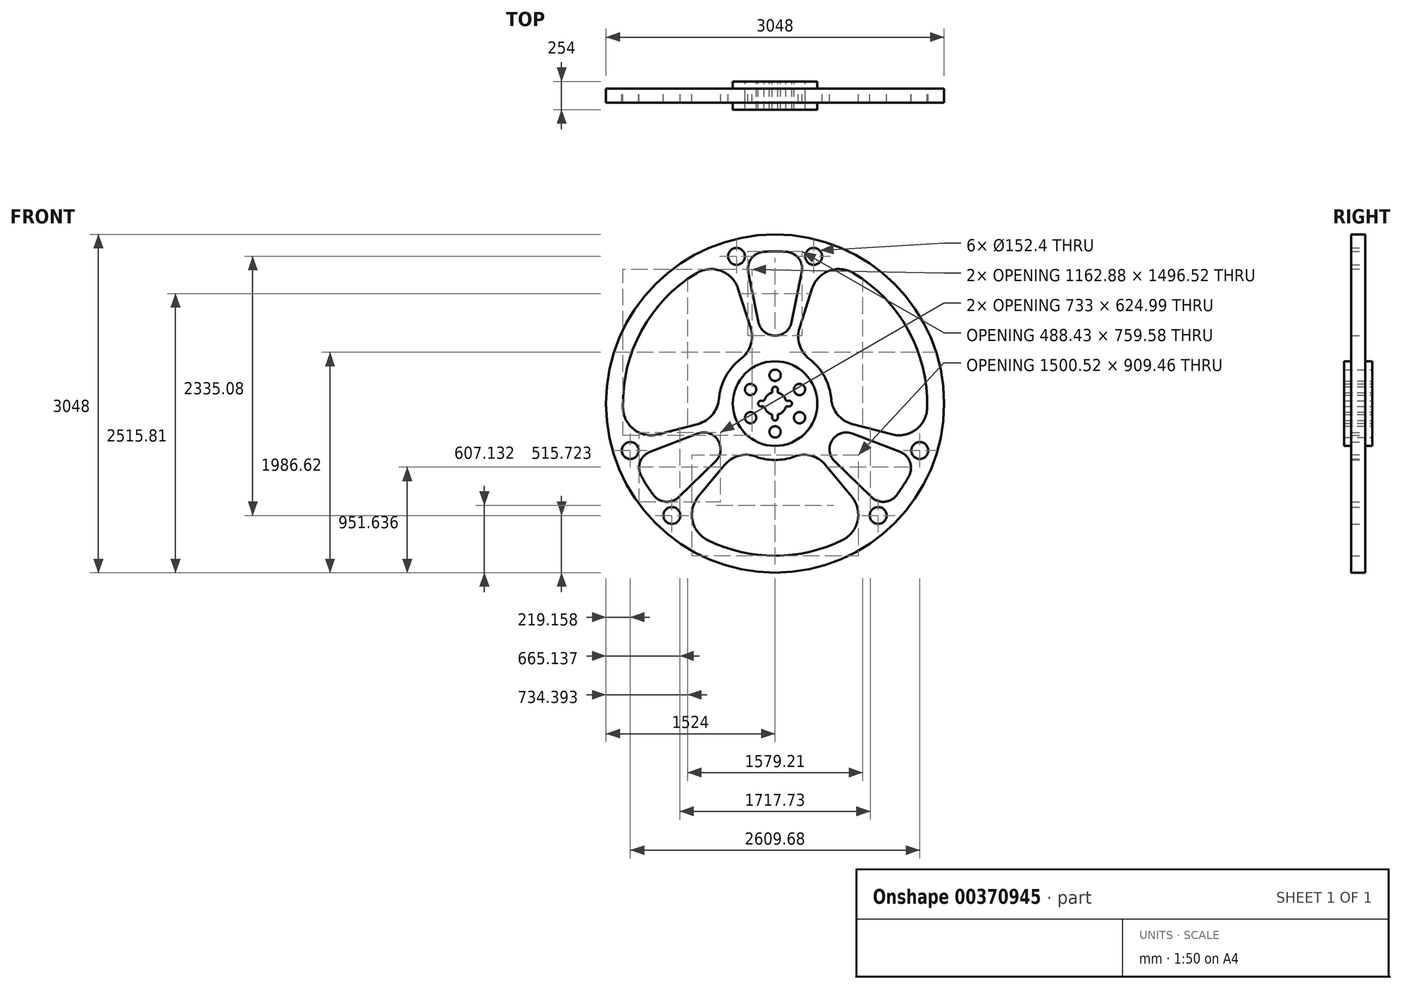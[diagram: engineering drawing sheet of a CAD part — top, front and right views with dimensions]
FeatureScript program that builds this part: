
annotation { "Feature Type Name" : "Feature", "Feature Type Description" : "" }
export const myFeature = defineFeature(function(context is Context, id is Id, definition is map)
    precondition{}
    {
        {
            var Q0;
            Q0=qCreatedBy(makeId("Front.planeOp"),FACE);
            var sketch = newSketch(context, id + "F0", { "sketchPlane" : qUnion([Q0])});
            skCircle(sketch, "E0", {"center": v(0, 0) * mm, "radius": 1524 * mm});
            skArc(sketch, "E1", {"start": v(-1207.5, -650.55) * mm, "mid": v(-1155.08, -739.64) * mm, "end": v(-1096.1, -824.54) * mm});
            skArc(sketch, "E2", {"start": v(-173.99, -477.28) * mm, "mid": v(0, -508) * mm, "end": v(173.99, -477.28) * mm});
            skCircle(sketch, "E3", {"center": v(-347.67, 1326.8) * mm, "radius": 76.2 * mm});
            skCircle(sketch, "E4", {"center": v(347.67, 1326.8) * mm, "radius": 76.2 * mm});
            skCircle(sketch, "E5", {"center": v(929.87, -1008.28) * mm, "radius": 76.2 * mm});
            skCircle(sketch, "E6", {"center": v(-929.87, -1008.28) * mm, "radius": 76.2 * mm});
            skCircle(sketch, "E7", {"center": v(-1304.84, -422.7) * mm, "radius": 76.2 * mm});
            skCircle(sketch, "E8", {"center": v(1304.84, -422.7) * mm, "radius": 76.2 * mm});
            skLineSegment(sketch, "E9", {"start": v(-420.82, 1305.45) * mm, "end": v(-419.52, 1301.42) * mm});
            skLineSegment(sketch, "E10", {"start": v(-273.45, 1344.06) * mm, "end": v(-272.6, 1339.92) * mm});
            skLineSegment(sketch, "E11", {"start": v(273.45, 1344.06) * mm, "end": v(272.6, 1339.92) * mm});
            skLineSegment(sketch, "E12", {"start": v(420.82, 1305.45) * mm, "end": v(419.52, 1301.42) * mm});
            skLineSegment(sketch, "E13", {"start": v(-1326.3, -349.58) * mm, "end": v(-1322.2, -348.5) * mm});
            skLineSegment(sketch, "E14", {"start": v(-1279.35, -494.5) * mm, "end": v(-1275.4, -492.98) * mm});
            skLineSegment(sketch, "E15", {"start": v(-984.43, -955.08) * mm, "end": v(-981.4, -952.13) * mm});
            skLineSegment(sketch, "E16", {"start": v(-872.44, -1058.36) * mm, "end": v(-869.75, -1055.1) * mm});
            skLineSegment(sketch, "E17", {"start": v(872.44, -1058.36) * mm, "end": v(869.75, -1055.1) * mm});
            skLineSegment(sketch, "E18", {"start": v(984.43, -955.08) * mm, "end": v(981.4, -952.13) * mm});
            skLineSegment(sketch, "E19", {"start": v(1279.35, -494.5) * mm, "end": v(1275.4, -492.98) * mm});
            skLineSegment(sketch, "E20", {"start": v(1326.3, -349.58) * mm, "end": v(1322.2, -348.5) * mm});
            skArc(sketch, "E21.trimOffspring", {"start": v(-609.08, -1228.95) * mm, "mid": v(0, -1371.6) * mm, "end": v(609.08, -1228.95) * mm});
            skArc(sketch, "E22.trimOffspring", {"start": v(1096.1, -824.54) * mm, "mid": v(1155.08, -739.64) * mm, "end": v(1207.5, -650.55) * mm});
            skArc(sketch, "E23.trimOffspring", {"start": v(1371.05, -39) * mm, "mid": v(1203.28, 658.33) * mm, "end": v(706.5, 1175.65) * mm});
            skArc(sketch, "E24.trimOffspring", {"start": v(103.3, 1367.7) * mm, "mid": v(0, 1371.6) * mm, "end": v(-103.3, 1367.7) * mm});
            skArc(sketch, "E25.trimOffspring", {"start": v(-706.5, 1175.65) * mm, "mid": v(-1203.28, 658.33) * mm, "end": v(-1371.05, -39) * mm});
            skArc(sketch, "E26.trimOffspring", {"start": v(-308.11, 403.9) * mm, "mid": v(-445.66, 243.83) * mm, "end": v(-506.29, 41.67) * mm});
            skArc(sketch, "E27.trimOffspring", {"start": v(506.29, 41.67) * mm, "mid": v(445.66, 243.83) * mm, "end": v(308.11, 403.9) * mm});
            skPoint(sketch, "E28.start.orphan", {"position": v(0, 1344.06) * mm});
            skArc(sketch, "E29", {"start": v(-103.3, 1367.7) * mm, "mid": v(-213.39, 1307.65) * mm, "end": v(-241.16, 1185.35) * mm});
            skArc(sketch, "E30", {"start": v(-333.92, 1035.86) * mm, "mid": v(-486.45, 1195.75) * mm, "end": v(-706.5, 1175.65) * mm});
            skArc(sketch, "E31", {"start": v(-1371.05, -39) * mm, "mid": v(-1269.3, -235.16) * mm, "end": v(-1052.41, -277.4) * mm});
            skArc(sketch, "E32", {"start": v(-1128.28, -436.12) * mm, "mid": v(-1216.3, -525.45) * mm, "end": v(-1207.5, -650.55) * mm});
            skArc(sketch, "E33", {"start": v(-1096.1, -824.54) * mm, "mid": v(-986.15, -884.86) * mm, "end": v(-868.19, -842.3) * mm});
            skArc(sketch, "E34", {"start": v(609.08, -1228.95) * mm, "mid": v(744.67, -1054.47) * mm, "end": v(692.28, -839.8) * mm});
            skArc(sketch, "E35", {"start": v(868.19, -842.3) * mm, "mid": v(986.15, -884.86) * mm, "end": v(1096.1, -824.54) * mm});
            skArc(sketch, "E36", {"start": v(1207.5, -650.55) * mm, "mid": v(1216.3, -525.45) * mm, "end": v(1128.28, -436.12) * mm});
            skArc(sketch, "E37", {"start": v(1052.41, -277.4) * mm, "mid": v(1269.3, -235.16) * mm, "end": v(1371.05, -39) * mm});
            skArc(sketch, "E38", {"start": v(706.5, 1175.65) * mm, "mid": v(486.45, 1195.75) * mm, "end": v(333.92, 1035.86) * mm});
            skArc(sketch, "E39", {"start": v(241.16, 1185.35) * mm, "mid": v(213.39, 1307.65) * mm, "end": v(103.3, 1367.7) * mm});
            skLineSegment(sketch, "E40.trimOffspring", {"start": v(-1052.41, -277.4) * mm, "end": v(-694.7, -183.1) * mm});
            skLineSegment(sketch, "E41.trimOffspring", {"start": v(-1128.28, -436.12) * mm, "end": v(-698.7, -270.07) * mm});
            skLineSegment(sketch, "E42.trimOffspring", {"start": v(-868.19, -842.3) * mm, "end": v(-537.63, -521.6) * mm});
            skLineSegment(sketch, "E43.trimOffspring", {"start": v(-692.28, -839.8) * mm, "end": v(-456.97, -554.35) * mm});
            skLineSegment(sketch, "E44.trimOffspring", {"start": v(692.28, -839.8) * mm, "end": v(456.97, -554.35) * mm});
            skLineSegment(sketch, "E45.trimOffspring", {"start": v(868.19, -842.3) * mm, "end": v(537.63, -521.6) * mm});
            skLineSegment(sketch, "E46.trimOffspring", {"start": v(1128.28, -436.12) * mm, "end": v(698.7, -270.07) * mm});
            skLineSegment(sketch, "E47.trimOffspring", {"start": v(1052.41, -277.4) * mm, "end": v(694.7, -183.1) * mm});
            skLineSegment(sketch, "E48.trimOffspring", {"start": v(333.92, 1035.86) * mm, "end": v(220.42, 683.77) * mm});
            skLineSegment(sketch, "E49.trimOffspring", {"start": v(241.16, 1185.35) * mm, "end": v(149.34, 734.03) * mm});
            skLineSegment(sketch, "E50.trimOffspring", {"start": v(-241.16, 1185.35) * mm, "end": v(-149.34, 734.03) * mm});
            skLineSegment(sketch, "E51.trimOffspring", {"start": v(-333.92, 1035.86) * mm, "end": v(-220.42, 683.77) * mm});
            skArc(sketch, "E52", {"start": v(-694.7, -183.1) * mm, "mid": v(-564.77, -100.66) * mm, "end": v(-506.29, 41.67) * mm});
            skArc(sketch, "E53", {"start": v(-308.11, 403.9) * mm, "mid": v(-219.79, 529.9) * mm, "end": v(-220.42, 683.77) * mm});
            skArc(sketch, "E54", {"start": v(220.42, 683.77) * mm, "mid": v(219.79, 529.9) * mm, "end": v(308.11, 403.9) * mm});
            skArc(sketch, "E55", {"start": v(506.29, 41.67) * mm, "mid": v(564.77, -100.66) * mm, "end": v(694.7, -183.1) * mm});
            skArc(sketch, "E56", {"start": v(456.97, -554.35) * mm, "mid": v(327.73, -470.84) * mm, "end": v(173.99, -477.28) * mm});
            skArc(sketch, "E57", {"start": v(-173.99, -477.28) * mm, "mid": v(-327.73, -470.84) * mm, "end": v(-456.97, -554.35) * mm});
            skArc(sketch, "E58", {"start": v(-537.63, -521.6) * mm, "mid": v(-515.4, -330.03) * mm, "end": v(-698.7, -270.07) * mm});
            skArc(sketch, "E59", {"start": v(-149.34, 734.03) * mm, "mid": v(0, 612.02) * mm, "end": v(149.34, 734.03) * mm});
            skArc(sketch, "E60.trimOffspring", {"start": v(-692.28, -839.8) * mm, "mid": v(-744.67, -1054.47) * mm, "end": v(-609.08, -1228.95) * mm});
            skCircle(sketch, "E61", {"center": v(0, 0) * mm, "radius": 381 * mm});
            skArc(sketch, "E62", {"start": v(698.7, -270.07) * mm, "mid": v(515.4, -330.03) * mm, "end": v(537.63, -521.6) * mm});
            skCircle(sketch, "E63", {"center": v(0, 254.8) * mm, "radius": 50.8 * mm});
            skCircle(sketch, "E64.1.0", {"center": v(-220.67, 127.4) * mm, "radius": 50.8 * mm});
            skCircle(sketch, "E64.2.0", {"center": v(-220.67, -127.4) * mm, "radius": 50.8 * mm});
            skCircle(sketch, "E64.3.0", {"center": v(0, -254.8) * mm, "radius": 50.8 * mm});
            skCircle(sketch, "E64.4.0", {"center": v(220.67, -127.4) * mm, "radius": 50.8 * mm});
            skCircle(sketch, "E64.5.0", {"center": v(220.67, 127.4) * mm, "radius": 50.8 * mm});
            skArc(sketch, "E65", {"start": v(-98.37, -25.4) * mm, "mid": v(-71.84, -71.84) * mm, "end": v(-25.4, -98.37) * mm});
            skArc(sketch, "E66", {"start": v(-127, 25.4) * mm, "mid": v(-152.4, 0) * mm, "end": v(-127, -25.4) * mm});
            skLineSegment(sketch, "E67", {"start": v(-127, 25.4) * mm, "end": v(-98.37, 25.4) * mm});
            skLineSegment(sketch, "E68", {"start": v(-127, -25.4) * mm, "end": v(-98.37, -25.4) * mm});
            skPoint(sketch, "E69.trimOffspring.end.orphan", {"position": v(-254, 0) * mm});
            skArc(sketch, "E70", {"start": v(-25.4, -127) * mm, "mid": v(0, -152.4) * mm, "end": v(25.4, -127) * mm});
            skLineSegment(sketch, "E71", {"start": v(25.4, -127) * mm, "end": v(25.4, -98.37) * mm});
            skLineSegment(sketch, "E72", {"start": v(-25.4, -127) * mm, "end": v(-25.4, -98.37) * mm});
            skArc(sketch, "E73.trimOffspring", {"start": v(25.4, -98.37) * mm, "mid": v(71.84, -71.84) * mm, "end": v(98.37, -25.4) * mm});
            skLineSegment(sketch, "E74", {"start": v(127, 25.4) * mm, "end": v(98.37, 25.4) * mm});
            skLineSegment(sketch, "E75", {"start": v(126.8, -25.4) * mm, "end": v(98.37, -25.4) * mm});
            skArc(sketch, "E76.trimOffspring", {"start": v(98.37, 25.4) * mm, "mid": v(71.84, 71.84) * mm, "end": v(25.4, 98.37) * mm});
            skArc(sketch, "E77.trimOffspring", {"start": v(126.8, -25.4) * mm, "mid": v(152.4, -0.1) * mm, "end": v(127, 25.4) * mm});
            skPoint(sketch, "E78.center.orphan", {"position": v(126.8, 0) * mm});
            skArc(sketch, "E79", {"start": v(25.4, 127) * mm, "mid": v(0, 152.4) * mm, "end": v(-25.4, 127) * mm});
            skLineSegment(sketch, "E80", {"start": v(-25.4, 127) * mm, "end": v(-25.4, 98.37) * mm});
            skLineSegment(sketch, "E81", {"start": v(25.4, 127) * mm, "end": v(25.4, 98.37) * mm});
            skArc(sketch, "E82.trimOffspring", {"start": v(-25.4, 98.37) * mm, "mid": v(-71.84, 71.84) * mm, "end": v(-98.37, 25.4) * mm});
            skSolve(sketch);
        }
        {
            var Q0;
            Q0=makeQuery(id+"F0.imprint","IMPRINT",FACE,{"disambiguationData":[TD([[makeQuery(id+"F0.imprint","IMPRINT",EDGE,{"derivedFrom":sQuery(id+"F0.wireOp",EDGE,"E0")}),1.0]])]});
            extrude(context, id + "F1", {"entities" : qUnion([Q0]), "depth" : 127 * mm, "symmetric" : true});
        }
        {
            var Q0;
            Q0=makeQuery(id+"F0.imprint","IMPRINT",FACE,{"disambiguationData":[TD([[makeQuery(id+"F0.imprint","IMPRINT",EDGE,{"derivedFrom":sQuery(id+"F0.wireOp",EDGE,"E61")}),1.0]])]});
            extrude(context, id + "F2", {"entities" : qUnion([Q0]), "operationType" : NewBodyOperationType.ADD, "depth" : 254 * mm, "symmetric" : true});
        }
    });
